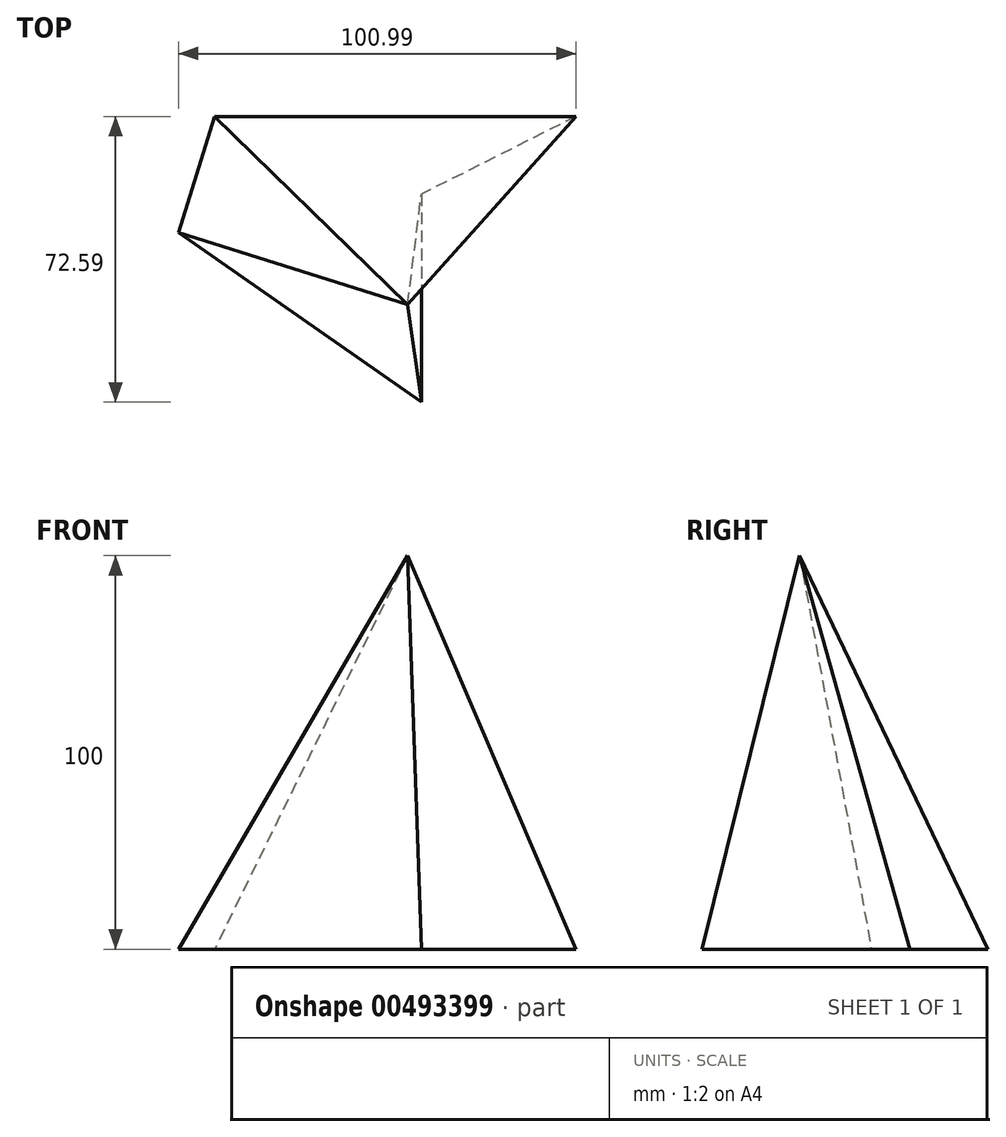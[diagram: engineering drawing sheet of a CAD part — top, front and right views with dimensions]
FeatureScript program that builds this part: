
annotation { "Feature Type Name" : "Feature", "Feature Type Description" : "" }
export const myFeature = defineFeature(function(context is Context, id is Id, definition is map)
    precondition{}
    {
        {
            var Q0;
            Q0=qCreatedBy(makeId("Top.planeOp"),FACE);
            var sketch = newSketch(context, id + "F0", { "sketchPlane" : qUnion([Q0])});
            skLineSegment(sketch, "E0", {"start": v(-49.06, 47.77) * mm, "end": v(42.75, 47.77) * mm});
            skLineSegment(sketch, "E1", {"start": v(42.75, 47.77) * mm, "end": v(3.44, 27.97) * mm});
            skLineSegment(sketch, "E2", {"start": v(3.44, 27.97) * mm, "end": v(3.44, -24.82) * mm});
            skLineSegment(sketch, "E3", {"start": v(3.44, -24.82) * mm, "end": v(-58.24, 18.22) * mm});
            skLineSegment(sketch, "E4", {"start": v(-58.24, 18.22) * mm, "end": v(-49.06, 47.77) * mm});
            skSolve(sketch);
        }
        {
            var Q0;
            Q0=qCreatedBy(makeId("Top.planeOp"),FACE);
            cPlane(context, id + "F1", {"entities" : qUnion([Q0]), "cplaneType" : CPlaneType.OFFSET, "offset" : 100 * mm, "width" : 150 * mm, "height" : 150 * mm});
        }
        {
            var Q0;
            Q0=qCreatedBy(id+"F1.planeOp",FACE);
            var sketch = newSketch(context, id + "F2", { "sketchPlane" : qUnion([Q0])});
            skPoint(sketch, "E5", {"position": v(0, 0) * mm});
            skSolve(sketch);
        }
        {
            var Q0;
            Q0=sQuery(id+"F2.wireOp",VERTEX,"E5");
            var Q1;
            Q1=makeQuery(id+"F0.imprint","IMPRINT",FACE,{"disambiguationData":[TD([[makeQuery(id+"F0.imprint","IMPRINT",EDGE,{"derivedFrom":sQuery(id+"F0.wireOp",EDGE,"E0")}),-1.0]])]});
            loft(context, id + "F3", {"sheetProfilesArray" : [{ "sheetProfileEntities" : qUnion([Q0]) }, { "sheetProfileEntities" : qUnion([Q1]) }]});
        }
    });
